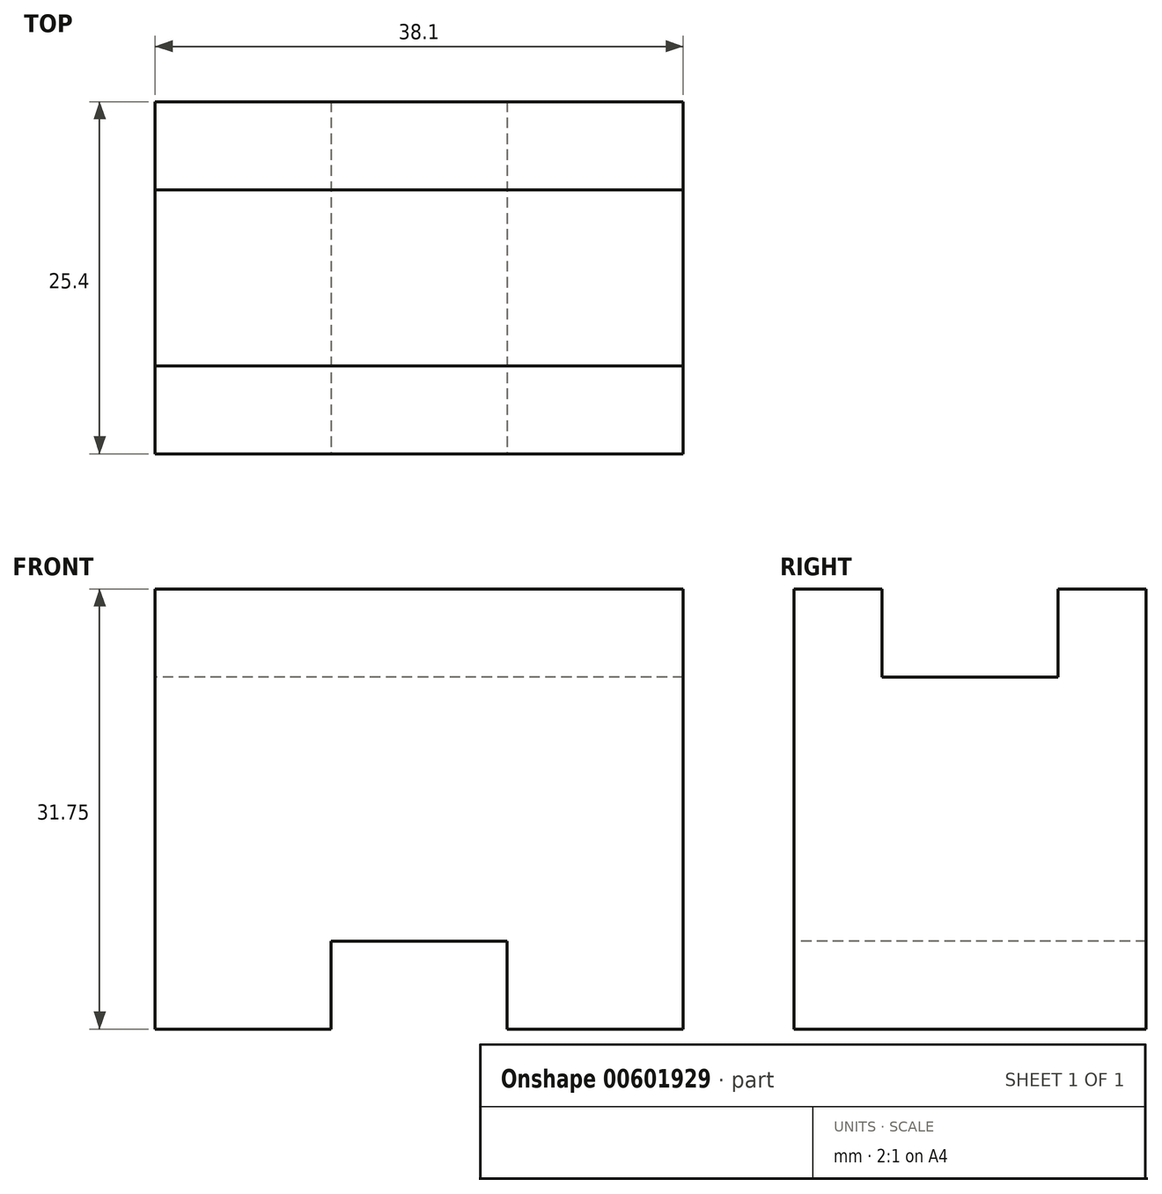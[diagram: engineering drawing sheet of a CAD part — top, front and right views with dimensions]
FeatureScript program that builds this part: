
annotation { "Feature Type Name" : "Feature", "Feature Type Description" : "" }
export const myFeature = defineFeature(function(context is Context, id is Id, definition is map)
    precondition{}
    {
        {
            var Q0;
            Q0=qCreatedBy(makeId("Right.planeOp"),FACE);
            var sketch = newSketch(context, id + "F0", { "sketchPlane" : qUnion([Q0])});
            skLineSegment(sketch, "E0", {"start": v(0, 0) * mm, "end": v(0, 31.75) * mm});
            skLineSegment(sketch, "E1", {"start": v(0, 31.75) * mm, "end": v(6.35, 31.75) * mm});
            skLineSegment(sketch, "E2", {"start": v(6.35, 31.75) * mm, "end": v(6.35, 25.4) * mm});
            skLineSegment(sketch, "E3", {"start": v(19.05, 25.4) * mm, "end": v(6.35, 25.4) * mm});
            skLineSegment(sketch, "E4", {"start": v(19.05, 25.4) * mm, "end": v(19.05, 31.75) * mm});
            skLineSegment(sketch, "E5", {"start": v(19.05, 31.75) * mm, "end": v(25.4, 31.75) * mm});
            skLineSegment(sketch, "E6", {"start": v(25.4, 31.75) * mm, "end": v(25.4, 0) * mm});
            skLineSegment(sketch, "E7", {"start": v(25.4, 0) * mm, "end": v(0, 0) * mm});
            skSolve(sketch);
        }
        {
            var Q0;
            Q0=makeQuery(id+"F0.imprint","IMPRINT",FACE,{"disambiguationData":[TD([[makeQuery(id+"F0.imprint","IMPRINT",EDGE,{"derivedFrom":sQuery(id+"F0.wireOp",EDGE,"E0")}),-1.0]])]});
            extrude(context, id + "F1", {"entities" : qUnion([Q0]), "depth" : 38.1 * mm, "offsetDistance" : 25.4 * mm});
        }
        {
            var Q0;
            Q0=makeQuery(id+"F1.opExtrude","SWEPT_FACE",FACE,{"disambiguationData":[OSD([sQuery(id+"F0.wireOp",EDGE,"E0")])]});
            var sketch = newSketch(context, id + "F2", { "sketchPlane" : qUnion([Q0])});
            skLineSegment(sketch, "E8", {"start": v(0, 0) * mm, "end": v(12.7, 0) * mm});
            skLineSegment(sketch, "E9", {"start": v(12.7, 0) * mm, "end": v(12.7, 6.35) * mm});
            skLineSegment(sketch, "E10", {"start": v(12.7, 6.35) * mm, "end": v(25.4, 6.35) * mm});
            skLineSegment(sketch, "E11", {"start": v(25.4, 6.35) * mm, "end": v(25.4, 0) * mm});
            skLineSegment(sketch, "E12", {"start": v(25.4, 0) * mm, "end": v(12.7, 0) * mm});
            skSolve(sketch);
        }
        {
            var Q0;
            Q0=makeQuery(id+"F2.imprint","IMPRINT",FACE,{"disambiguationData":[TD([[makeQuery(id+"F2.imprint","IMPRINT",EDGE,{"derivedFrom":sQuery(id+"F2.wireOp",EDGE,"E9")}),-1.0]])]});
            extrude(context, id + "F3", {"entities" : qUnion([Q0]), "operationType" : NewBodyOperationType.REMOVE, "oppositeDirection" : true, "depth" : 25.4 * mm, "offsetDistance" : 25.4 * mm});
        }
    });
